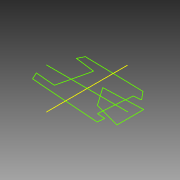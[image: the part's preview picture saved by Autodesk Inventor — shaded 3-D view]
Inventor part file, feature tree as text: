
AUTODESK INVENTOR PART (.ipt)
format: ipt  version: 2015 (Build 190159000, 159)  size: 62,976 bytes
history: native  units: mm
features: sketch x1
ambient origin geometry x8: Origin, YZ Plane, XZ Plane, XY Plane, X Axis, Y Axis, Z Axis, Center Point
feature tree (1):
  sketch  "Sketch1"
